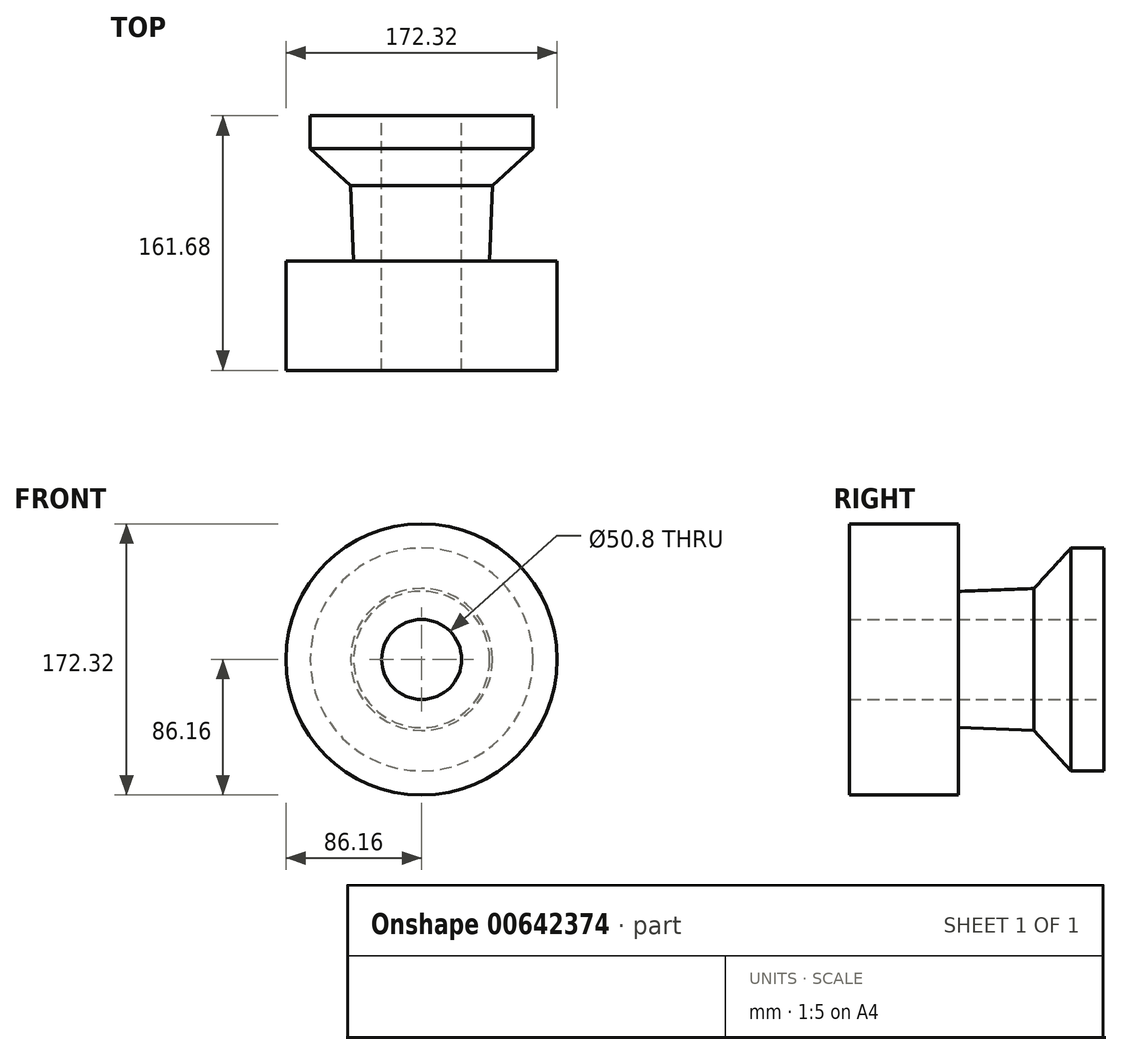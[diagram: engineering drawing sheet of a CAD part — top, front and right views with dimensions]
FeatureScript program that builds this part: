
annotation { "Feature Type Name" : "Feature", "Feature Type Description" : "" }
export const myFeature = defineFeature(function(context is Context, id is Id, definition is map)
    precondition{}
    {
        {
            var Q0;
            Q0=qCreatedBy(makeId("Top.planeOp"),FACE);
            var sketch = newSketch(context, id + "F0", { "sketchPlane" : qUnion([Q0])});
            skLineSegment(sketch, "E0", {"start": v(0, 0) * mm, "end": v(86.16, 0) * mm});
            skLineSegment(sketch, "E1", {"start": v(86.16, 0) * mm, "end": v(86.16, 69.3) * mm});
            skLineSegment(sketch, "E2", {"start": v(86.16, 69.3) * mm, "end": v(43.26, 69.3) * mm});
            skLineSegment(sketch, "E3", {"start": v(43.26, 69.3) * mm, "end": v(45.1, 117.32) * mm});
            skLineSegment(sketch, "E4", {"start": v(45.1, 117.32) * mm, "end": v(70.76, 140.78) * mm});
            skLineSegment(sketch, "E5", {"start": v(70.76, 140.78) * mm, "end": v(70.76, 161.68) * mm});
            skLineSegment(sketch, "E6", {"start": v(70.76, 161.68) * mm, "end": v(0, 161.68) * mm});
            skLineSegment(sketch, "E7", {"start": v(0, 161.68) * mm, "end": v(0, 0) * mm});
            skSolve(sketch);
        }
        {
            var Q0;
            Q0=makeQuery(id+"F0.imprint","IMPRINT",FACE,{"disambiguationData":[TD([[makeQuery(id+"F0.imprint","IMPRINT",EDGE,{"derivedFrom":sQuery(id+"F0.wireOp",EDGE,"E0")}),1.0]])]});
            var Q1;
            Q1=sQuery(id+"F0.wireOp",EDGE,"E7");
            revolve(context, id + "F1", {"entities" : qUnion([Q0]), "axis" : qUnion([Q1]), "revolveType" : RevolveType.FULL});
        }
        {
            var Q0;
            Q0=makeQuery(id+"F1.opRevolve","SWEPT_FACE",FACE,{"disambiguationData":[OSD([sQuery(id+"F0.wireOp",EDGE,"E6")])]});
            var sketch = newSketch(context, id + "F2", { "sketchPlane" : qUnion([Q0])});
            skPoint(sketch, "E8", {"position": v(0, 0) * mm});
            skSolve(sketch);
        }
        {
            var Q0;
            Q0=sQuery(id+"F2.wireOp",VERTEX,"E8");
            var Q1;
            Q1=makeQuery(id+"F1.opRevolve","SWEPT_BODY",BODY,{"disambiguationData":[OSD([sQuery(id+"F0.wireOp",EDGE,"E0"),sQuery(id+"F0.wireOp",EDGE,"E1"),sQuery(id+"F0.wireOp",EDGE,"E2"),sQuery(id+"F0.wireOp",EDGE,"E3"),sQuery(id+"F0.wireOp",EDGE,"E4"),sQuery(id+"F0.wireOp",EDGE,"E5"),sQuery(id+"F0.wireOp",EDGE,"E6"),sQuery(id+"F0.wireOp",EDGE,"E7")])]});
            hole(context, id + "F3", {"style" : HoleStyle.SIMPLE, "endStyle" : HoleEndStyle.THROUGH, "holeDiameter" : 50.8 * mm, "majorDiameter" : 6.35 * mm, "isTappedThrough" : true, "tappedDepth" : 12.7 * mm, "tapClearance" : 3, "locations" : qUnion([Q0]), "scope" : qUnion([Q1])});
        }
    });
